# Revit family: Secador de Manos MB-1012 0
name_source: partatom
category: Plumbing Fixtures
revit_build: Autodesk Revit 2015 (Build: 20140223_1515(x64)
units: mm (PartAtom-declared; Revit-internal decimal feet)

## types (1)
- MB-1012
    Air Flow = 0 m³/h
    Air Temperature to 4" = 55 °C
    Air Velocity = 90.0 m/s
    Automatic Shut Off = 60.0 s
    Current Consumption = 8 A
    Default Elevation = 53 "
    Description = Incluye Herramienta y Paquete de Sujeción, Opera con un Sensor Infrarrojo, Conexión Monofásica a 120 Vca
    Drying Time = 15.0 s
    Electrical Protection = Restored Auto Thermostat Engin Blows at 105°C
    Manufacturer = HELVEX S.A. DE C.V.
    Model = MB-1012
    Noise = 78 dB
    Power Consumption = 1000 VA
    Range Of Activation = Self-Adjusting 180 mm Max.
    Stainless Steel = Stainless Steel
    Total Depth = 5.4 "
    Total Height = 7.1 "
    Total Length = 9.8 "
    Type Comments = Secador de Manos Turbo
    Type Image = MB-1012.jpg
    URL = http://www.helvex.com.mx
    Voltage = 120 V
    Voltage 2 = 60

note: source unit labels omitted for Voltage 2 — the stored unit's dimension contradicts the parameter name (converter mislabeling)

## geometry (parser evidence)
native form markers: Sweep x8
no freeform markers — native parametric forms only
